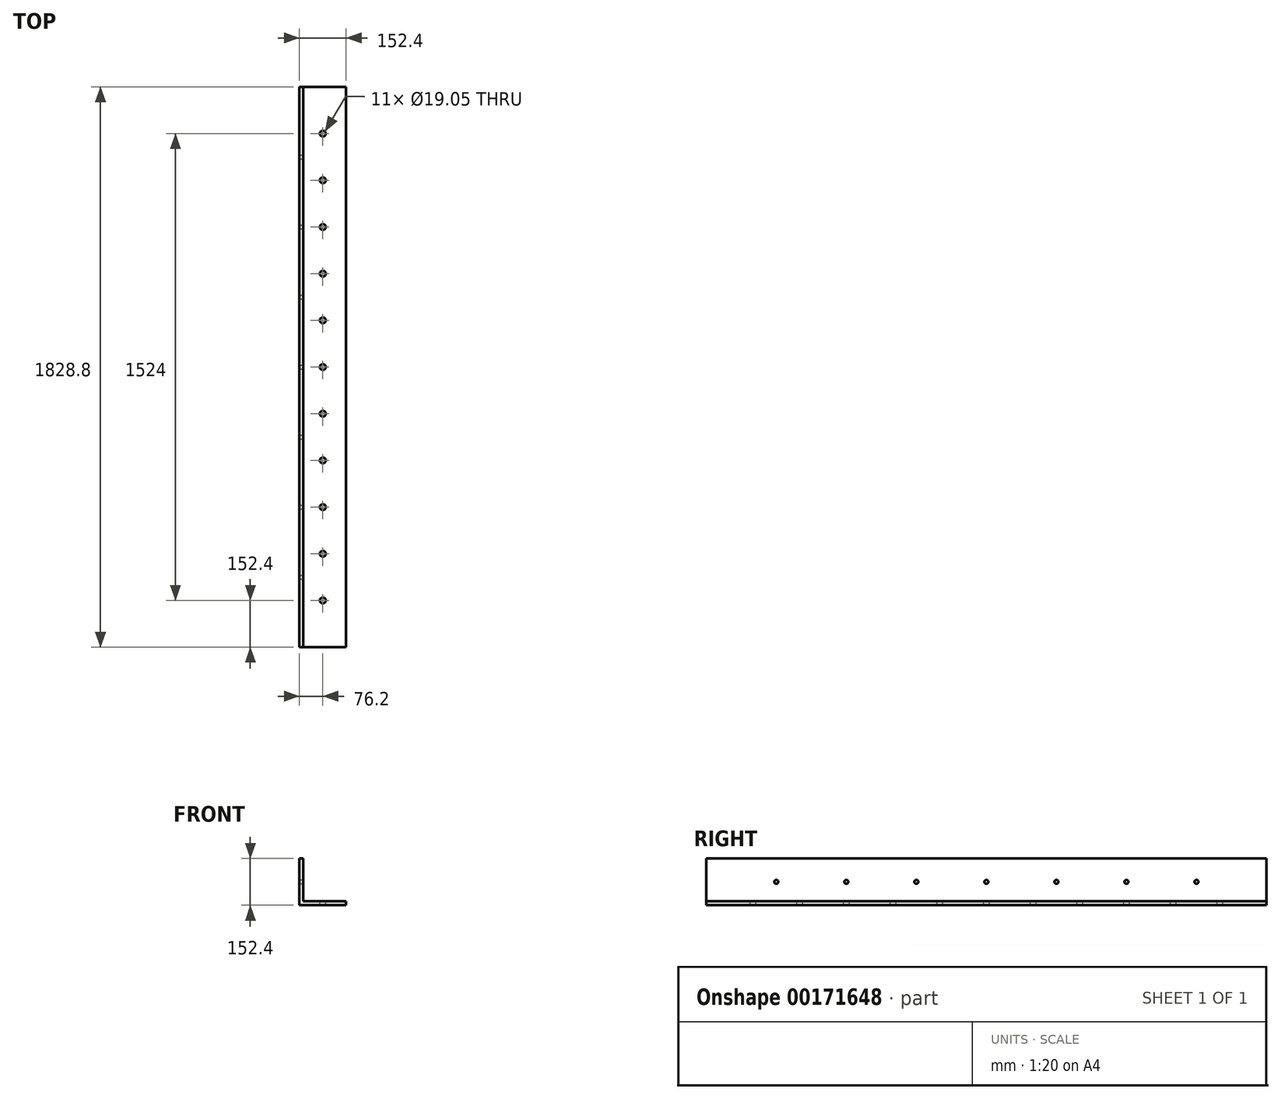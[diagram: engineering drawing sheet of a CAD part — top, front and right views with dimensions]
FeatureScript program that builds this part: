
annotation { "Feature Type Name" : "Feature", "Feature Type Description" : "" }
export const myFeature = defineFeature(function(context is Context, id is Id, definition is map)
    precondition{}
    {
        {
            var Q0;
            Q0=qCreatedBy(makeId("Front.planeOp"),FACE);
            var sketch = newSketch(context, id + "F0", { "sketchPlane" : qUnion([Q0])});
            skLineSegment(sketch, "E0.bottom", {"start": v(-6.35, 152.4) * mm, "end": v(6.35, 152.4) * mm});
            skLineSegment(sketch, "E0.top", {"start": v(-6.35, 0) * mm, "end": v(6.35, 0) * mm});
            skLineSegment(sketch, "E0.left", {"start": v(-6.35, 152.4) * mm, "end": v(-6.35, 0) * mm});
            skLineSegment(sketch, "E0.right", {"start": v(6.35, 152.4) * mm, "end": v(6.35, 12.7) * mm});
            skLineSegment(sketch, "E1.bottom", {"start": v(0, 0) * mm, "end": v(146.05, 0) * mm});
            skLineSegment(sketch, "E1.top", {"start": v(6.35, 12.7) * mm, "end": v(146.05, 12.7) * mm});
            skLineSegment(sketch, "E1.right", {"start": v(146.05, 0) * mm, "end": v(146.05, 12.7) * mm});
            skSolve(sketch);
        }
        {
            var Q0;
            Q0=makeQuery(id+"F0.imprint","IMPRINT",FACE,{"disambiguationData":[TD([[makeQuery(id+"F0.imprint","IMPRINT",EDGE,{"derivedFrom":sQuery(id+"F0.wireOp",EDGE,"E0.bottom")}),-1.0]])]});
            extrude(context, id + "F1", {"entities" : qUnion([Q0]), "depth" : 1828.8 * mm});
        }
        {
            var Q0;
            Q0=makeQuery(id+"F1.opExtrude","SWEPT_FACE",FACE,{"disambiguationData":[OSD([sQuery(id+"F0.wireOp",EDGE,"E0.top"),sQuery(id+"F0.wireOp",EDGE,"E1.bottom")])]});
            var sketch = newSketch(context, id + "F2", { "sketchPlane" : qUnion([Q0])});
            skPoint(sketch, "E2", {"position": v(69.85, 1676.4) * mm});
            skPoint(sketch, "E3", {"position": v(69.85, 1524) * mm});
            skPoint(sketch, "E4", {"position": v(69.85, 1371.6) * mm});
            skPoint(sketch, "E5", {"position": v(69.85, 1219.2) * mm});
            skPoint(sketch, "E6", {"position": v(69.85, 1066.8) * mm});
            skPoint(sketch, "E7", {"position": v(69.85, 914.4) * mm});
            skPoint(sketch, "E8", {"position": v(69.85, 762) * mm});
            skPoint(sketch, "E9", {"position": v(69.85, 609.6) * mm});
            skPoint(sketch, "E10", {"position": v(69.85, 457.2) * mm});
            skPoint(sketch, "E11", {"position": v(69.85, 304.8) * mm});
            skPoint(sketch, "E12", {"position": v(69.85, 152.4) * mm});
            skSolve(sketch);
        }
        {
            var Q0;
            Q0=makeQuery(id+"F1.opExtrude","SWEPT_FACE",FACE,{"disambiguationData":[OSD([sQuery(id+"F0.wireOp",EDGE,"E0.left")])]});
            var sketch = newSketch(context, id + "F3", { "sketchPlane" : qUnion([Q0])});
            skPoint(sketch, "E13", {"position": v(1371.6, 76.2) * mm});
            skPoint(sketch, "E14", {"position": v(1600.2, 76.2) * mm});
            skPoint(sketch, "E15", {"position": v(1143, 76.2) * mm});
            skPoint(sketch, "E16", {"position": v(914.4, 76.2) * mm});
            skPoint(sketch, "E17", {"position": v(685.8, 76.2) * mm});
            skPoint(sketch, "E18", {"position": v(457.2, 76.2) * mm});
            skPoint(sketch, "E19", {"position": v(228.6, 76.2) * mm});
            skSolve(sketch);
        }
        {
            var Q0;
            Q0=sQuery(id+"F2.wireOp",VERTEX,"E6");
            var Q1;
            Q1=sQuery(id+"F2.wireOp",VERTEX,"E5");
            var Q2;
            Q2=sQuery(id+"F2.wireOp",VERTEX,"E4");
            var Q3;
            Q3=sQuery(id+"F2.wireOp",VERTEX,"E3");
            var Q4;
            Q4=sQuery(id+"F2.wireOp",VERTEX,"E2");
            var Q5;
            Q5=sQuery(id+"F2.wireOp",VERTEX,"E7");
            var Q6;
            Q6=sQuery(id+"F2.wireOp",VERTEX,"E8");
            var Q7;
            Q7=sQuery(id+"F2.wireOp",VERTEX,"E9");
            var Q8;
            Q8=sQuery(id+"F2.wireOp",VERTEX,"E10");
            var Q9;
            Q9=sQuery(id+"F2.wireOp",VERTEX,"E11");
            var Q10;
            Q10=sQuery(id+"F2.wireOp",VERTEX,"E12");
            var Q11;
            Q11=makeQuery(id+"F1.opExtrude","SWEPT_BODY",BODY,{"disambiguationData":[OSD([sQuery(id+"F0.wireOp",EDGE,"E0.bottom"),sQuery(id+"F0.wireOp",EDGE,"E0.top"),sQuery(id+"F0.wireOp",EDGE,"E0.left"),sQuery(id+"F0.wireOp",EDGE,"E0.right"),sQuery(id+"F0.wireOp",EDGE,"E1.bottom"),sQuery(id+"F0.wireOp",EDGE,"E1.top"),sQuery(id+"F0.wireOp",EDGE,"E1.right")])]});
            hole(context, id + "F4", {"style" : HoleStyle.SIMPLE, "endStyle" : HoleEndStyle.THROUGH, "holeDiameter" : 19.05 * mm, "locations" : qUnion([Q0, Q1, Q2, Q3, Q4, Q5, Q6, Q7, Q8, Q9, Q10]), "scope" : qUnion([Q11]), "isTappedThrough" : true});
        }
        {
            var Q0;
            Q0=sQuery(id+"F3.wireOp",VERTEX,"E14");
            var Q1;
            Q1=sQuery(id+"F3.wireOp",VERTEX,"E13");
            var Q2;
            Q2=sQuery(id+"F3.wireOp",VERTEX,"E15");
            var Q3;
            Q3=sQuery(id+"F3.wireOp",VERTEX,"E16");
            var Q4;
            Q4=sQuery(id+"F3.wireOp",VERTEX,"E17");
            var Q5;
            Q5=sQuery(id+"F3.wireOp",VERTEX,"E18");
            var Q6;
            Q6=sQuery(id+"F3.wireOp",VERTEX,"E19");
            var Q7;
            Q7=makeQuery(id+"F1.opExtrude","SWEPT_BODY",BODY,{"disambiguationData":[OSD([sQuery(id+"F0.wireOp",EDGE,"E0.bottom"),sQuery(id+"F0.wireOp",EDGE,"E0.top"),sQuery(id+"F0.wireOp",EDGE,"E0.left"),sQuery(id+"F0.wireOp",EDGE,"E0.right"),sQuery(id+"F0.wireOp",EDGE,"E1.bottom"),sQuery(id+"F0.wireOp",EDGE,"E1.top"),sQuery(id+"F0.wireOp",EDGE,"E1.right")])]});
            hole(context, id + "F5", {"style" : HoleStyle.SIMPLE, "endStyle" : HoleEndStyle.THROUGH, "holeDiameter" : 12.7 * mm, "locations" : qUnion([Q0, Q1, Q2, Q3, Q4, Q5, Q6]), "scope" : qUnion([Q7]), "isTappedThrough" : true});
        }
    });
